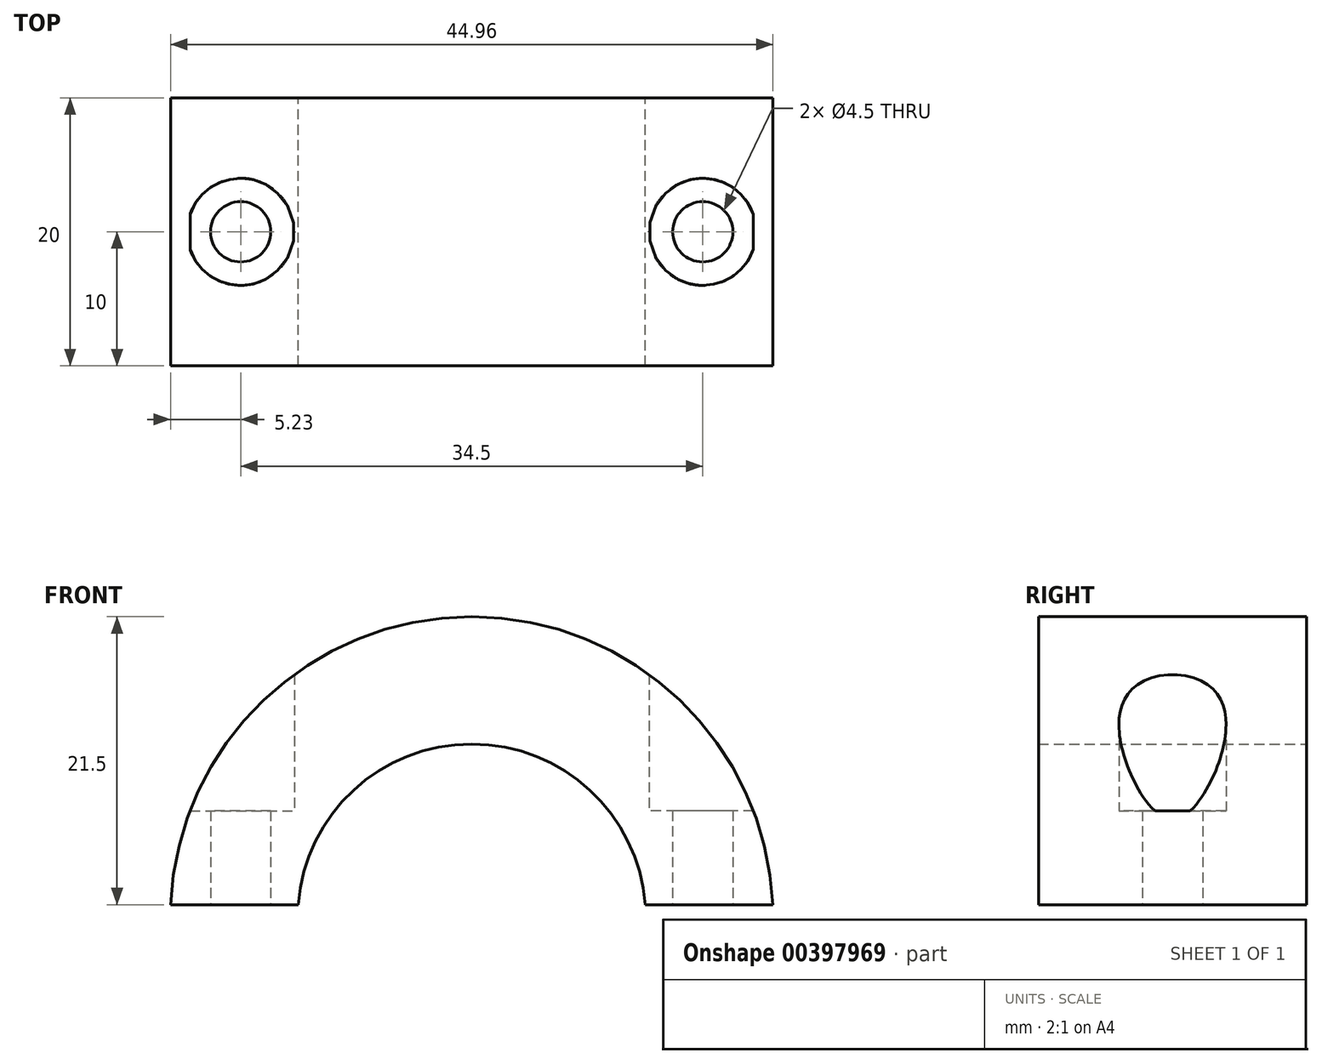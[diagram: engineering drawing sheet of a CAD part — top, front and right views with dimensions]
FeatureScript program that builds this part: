
annotation { "Feature Type Name" : "Feature", "Feature Type Description" : "" }
export const myFeature = defineFeature(function(context is Context, id is Id, definition is map)
    precondition{}
    {
        {
            var Q0;
            Q0=qCreatedBy(makeId("Front.planeOp"),FACE);
            var sketch = newSketch(context, id + "F0", { "sketchPlane" : qUnion([Q0])});
            skArc(sketch, "E0", {"start": v(12.96, 1) * mm, "mid": v(0, 13) * mm, "end": v(-12.96, 1) * mm});
            skLineSegment(sketch, "E1", {"start": v(0, 0) * mm, "end": v(24.3, 0) * mm, "construction": true});
            skLineSegment(sketch, "E2", {"start": v(-22.48, 1) * mm, "end": v(-12.96, 1) * mm});
            skArc(sketch, "E3", {"start": v(22.48, 1) * mm, "mid": v(0, 22.5) * mm, "end": v(-22.48, 1) * mm});
            skLineSegment(sketch, "E4.trimOffspring", {"start": v(12.96, 1) * mm, "end": v(22.48, 1) * mm});
            skSolve(sketch);
        }
        {
            var Q0;
            Q0 = qSketchRegion(id + "F0", true);
            extrude(context, id + "F1", {"entities" : qUnion([Q0]), "depth" : 20 * mm});
        }
        {
            var Q0;
            Q0=makeQuery(id+"F1.opExtrude","SWEPT_FACE",FACE,{"disambiguationData":[OSD([sQuery(id+"F0.wireOp",EDGE,"E2")])]});
            var sketch = newSketch(context, id + "F2", { "sketchPlane" : qUnion([Q0])});
            skLineSegment(sketch, "E5", {"start": v(-22.48, 10) * mm, "end": v(22.48, 10) * mm, "construction": true});
            skPoint(sketch, "E5.endSnap0", {"position": v(-12.96, 10) * mm});
            skCircle(sketch, "E6", {"center": v(-17.25, 10) * mm, "radius": 2.25 * mm});
            skLineSegment(sketch, "E7", {"start": v(0, -566.64) * mm, "end": v(0, 0) * mm, "construction": true});
            skPoint(sketch, "E7.endSnap0", {"position": v(0, 10) * mm});
            skCircle(sketch, "E8.MirrorC", {"center": v(17.25, 10) * mm, "radius": 2.25 * mm});
            skSolve(sketch);
        }
        {
            var Q0;
            Q0 = qSketchRegion(id + "F2", true);
            extrude(context, id + "F3", {"entities" : qUnion([Q0]), "operationType" : NewBodyOperationType.REMOVE, "endBound" : BoundingType.THROUGH_ALL, "oppositeDirection" : true, "depth" : 25 * mm});
        }
        {
            var Q0;
            Q0=qCreatedBy(makeId("Top.planeOp"),FACE);
            cPlane(context, id + "F4", {"entities" : qUnion([Q0]), "cplaneType" : CPlaneType.OFFSET, "offset" : 8 * mm, "width" : 150 * mm, "height" : 150 * mm});
        }
        {
            var Q0;
            Q0=qCreatedBy(id+"F4.planeOp",FACE);
            var sketch = newSketch(context, id + "F5", { "sketchPlane" : qUnion([Q0])});
            skCircle(sketch, "E9", {"center": v(-17.25, -10) * mm, "radius": 4 * mm});
            skLineSegment(sketch, "E10", {"start": v(0, 0) * mm, "end": v(0, 20.8) * mm, "construction": true});
            skCircle(sketch, "E11.MirrorC", {"center": v(17.25, -10) * mm, "radius": 4 * mm});
            skSolve(sketch);
        }
        {
            var Q0;
            Q0 = qSketchRegion(id + "F5", true);
            extrude(context, id + "F6", {"entities" : qUnion([Q0]), "operationType" : NewBodyOperationType.REMOVE, "endBound" : BoundingType.THROUGH_ALL, "depth" : 25 * mm});
        }
    });
